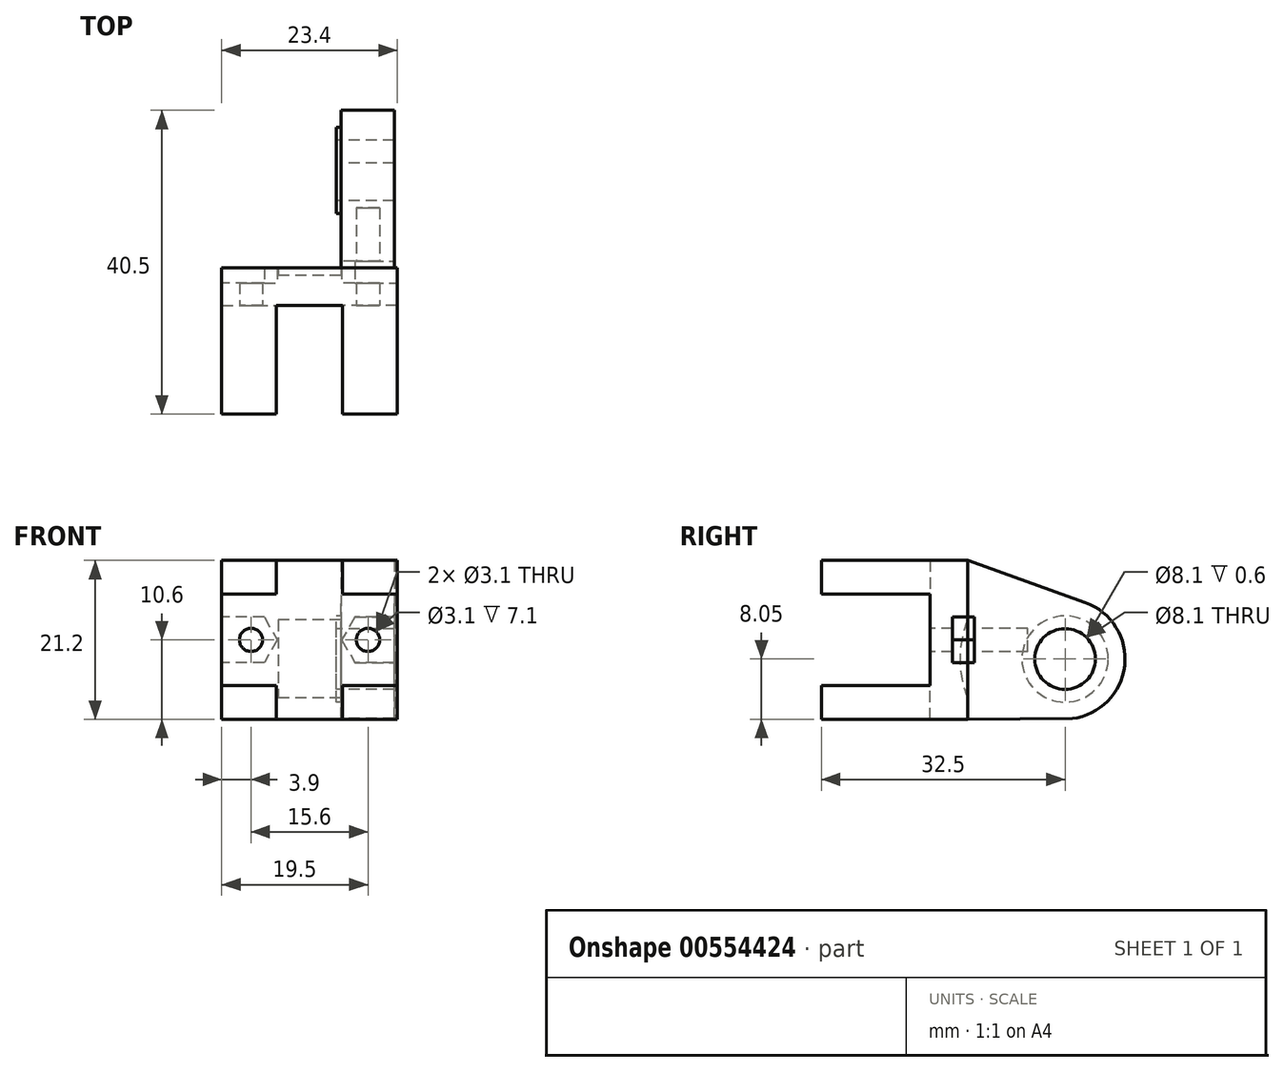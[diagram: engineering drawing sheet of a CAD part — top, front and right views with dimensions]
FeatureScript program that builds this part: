
annotation { "Feature Type Name" : "Feature", "Feature Type Description" : "" }
export const myFeature = defineFeature(function(context is Context, id is Id, definition is map)
    precondition{}
    {
        {
            assignVariable(context, id + "F0", {"name" : "bearing_width", "anyValue" : 7.2});
        }
        {
            assignVariable(context, id + "F1", {"name" : "bearing_bump", "anyValue" : 0.6});
        }
        {
            var Q0;
            Q0=qCreatedBy(makeId("Front.planeOp"),FACE);
            var sketch = newSketch(context, id + "F2", { "sketchPlane" : qUnion([Q0])});
            skLineSegment(sketch, "E0.bottom", {"start": v(-11.7, 10.6) * mm, "end": v(11.7, 10.6) * mm});
            skLineSegment(sketch, "E0.top", {"start": v(-11.7, -10.6) * mm, "end": v(11.7, -10.6) * mm});
            skLineSegment(sketch, "E0.left", {"start": v(-11.7, 10.6) * mm, "end": v(-11.7, -10.6) * mm});
            skLineSegment(sketch, "E0.right", {"start": v(11.7, 10.6) * mm, "end": v(11.7, -10.6) * mm});
            skPoint(sketch, "E0.middle", {"position": v(0, 0) * mm});
            skSolve(sketch);
        }
        {
            var Q0;
            Q0=qSketchRegion(id+"F2",true);
            extrude(context, id + "F3", {"entities" : qUnion([Q0]), "depth" : 5 * mm, "offsetDistance" : 25 * mm});
        }
        {
            var Q0;
            Q0=makeQuery(id+"F3.opExtrude","CAP_FACE",FACE,{"disambiguationData":[OSD([sQuery(id+"F2.wireOp",EDGE,"E0.bottom"),sQuery(id+"F2.wireOp",EDGE,"E0.top"),sQuery(id+"F2.wireOp",EDGE,"E0.left"),sQuery(id+"F2.wireOp",EDGE,"E0.right")])],"isStart":false});
            var sketch = newSketch(context, id + "F4", { "sketchPlane" : qUnion([Q0])});
            skCircle(sketch, "E1", {"center": v(-7.8, 0) * mm, "radius": 1.55 * mm});
            skCircle(sketch, "E2", {"center": v(7.8, 0) * mm, "radius": 1.55 * mm});
            skSolve(sketch);
        }
        {
            var Q0;
            Q0=makeQuery(id+"F3.opExtrude","CAP_FACE",FACE,{"disambiguationData":[OSD([sQuery(id+"F2.wireOp",EDGE,"E0.bottom"),sQuery(id+"F2.wireOp",EDGE,"E0.top"),sQuery(id+"F2.wireOp",EDGE,"E0.left"),sQuery(id+"F2.wireOp",EDGE,"E0.right")])],"isStart":false});
            var sketch = newSketch(context, id + "F5", { "sketchPlane" : qUnion([Q0])});
            skLineSegment(sketch, "E3.bottom", {"start": v(-11.7, 10.6) * mm, "end": v(-4.4, 10.6) * mm});
            skLineSegment(sketch, "E3.top", {"start": v(-11.7, 6.1) * mm, "end": v(-4.4, 6.1) * mm});
            skLineSegment(sketch, "E3.left", {"start": v(-11.7, 10.6) * mm, "end": v(-11.7, 6.1) * mm});
            skLineSegment(sketch, "E3.right", {"start": v(-4.4, 10.6) * mm, "end": v(-4.4, 6.1) * mm});
            skLineSegment(sketch, "E4.bottom", {"start": v(11.7, 10.6) * mm, "end": v(4.4, 10.6) * mm});
            skLineSegment(sketch, "E4.top", {"start": v(11.7, 6.1) * mm, "end": v(4.4, 6.1) * mm});
            skLineSegment(sketch, "E4.left", {"start": v(11.7, 10.6) * mm, "end": v(11.7, 6.1) * mm});
            skLineSegment(sketch, "E4.right", {"start": v(4.4, 10.6) * mm, "end": v(4.4, 6.1) * mm});
            skLineSegment(sketch, "E5.bottom", {"start": v(-11.7, -10.6) * mm, "end": v(-4.4, -10.6) * mm});
            skLineSegment(sketch, "E5.top", {"start": v(-11.7, -6.1) * mm, "end": v(-4.4, -6.1) * mm});
            skLineSegment(sketch, "E5.left", {"start": v(-11.7, -10.6) * mm, "end": v(-11.7, -6.1) * mm});
            skLineSegment(sketch, "E5.right", {"start": v(-4.4, -10.6) * mm, "end": v(-4.4, -6.1) * mm});
            skLineSegment(sketch, "E6.bottom", {"start": v(11.7, -10.6) * mm, "end": v(4.4, -10.6) * mm});
            skLineSegment(sketch, "E6.top", {"start": v(11.7, -6.1) * mm, "end": v(4.4, -6.1) * mm});
            skLineSegment(sketch, "E6.left", {"start": v(11.7, -10.6) * mm, "end": v(11.7, -6.1) * mm});
            skLineSegment(sketch, "E6.right", {"start": v(4.4, -10.6) * mm, "end": v(4.4, -6.1) * mm});
            skSolve(sketch);
        }
        {
            var Q0;
            Q0=qSketchRegion(id+"F5",true);
            extrude(context, id + "F6", {"entities" : qUnion([Q0]), "operationType" : NewBodyOperationType.ADD, "depth" : 14.5 * mm, "offsetDistance" : 25 * mm});
        }
        {
            var Q0;
            Q0=makeQuery(id+"F4.imprint","IMPRINT",FACE,{"disambiguationData":[TD([[makeQuery(id+"F4.imprint","IMPRINT",EDGE,{"derivedFrom":sQuery(id+"F4.wireOp",EDGE,"E1")}),-1.0]])]});
            var sketch = newSketch(context, id + "F7", { "sketchPlane" : qUnion([Q0])});
            skCircle(sketch, "E7.cCircle", {"center": v(-7.8, 0) * mm, "radius": 3.5 * mm, "construction": true});
            skLineSegment(sketch, "E7.4", {"start": v(-6.05, 3.03) * mm, "end": v(-4.3, 0) * mm});
            skLineSegment(sketch, "E7.5", {"start": v(-4.3, 0) * mm, "end": v(-6.05, -3.03) * mm});
            skLineSegment(sketch, "E8.bottom", {"start": v(-6.05, 3.03) * mm, "end": v(-11.7, 3.03) * mm});
            skLineSegment(sketch, "E8.top", {"start": v(-6.05, -3.03) * mm, "end": v(-11.7, -3.03) * mm});
            skLineSegment(sketch, "E8.right", {"start": v(-11.7, 3.03) * mm, "end": v(-11.7, -3.03) * mm});
            skLineSegment(sketch, "E9.MirrorCS", {"start": v(6.05, 3.03) * mm, "end": v(4.3, 0) * mm});
            skCircle(sketch, "E10.MirrorC", {"center": v(7.8, 0) * mm, "radius": 3.5 * mm, "construction": true});
            skLineSegment(sketch, "E11.MirrorCS", {"start": v(6.05, -3.03) * mm, "end": v(11.7, -3.03) * mm});
            skLineSegment(sketch, "E12.MirrorCS", {"start": v(11.7, 3.03) * mm, "end": v(11.7, -3.03) * mm});
            skLineSegment(sketch, "E13.MirrorCS", {"start": v(6.05, 3.03) * mm, "end": v(11.7, 3.03) * mm});
            skLineSegment(sketch, "E14.MirrorCS", {"start": v(4.3, 0) * mm, "end": v(6.05, -3.03) * mm});
            skSolve(sketch);
        }
        {
            var Q0;
            Q0=qCreatedBy(makeId("Right.planeOp"),FACE);
            var sketch = newSketch(context, id + "F8", { "sketchPlane" : qUnion([Q0])});
            skCircle(sketch, "E15", {"center": v(13, -2.55) * mm, "radius": 4.05 * mm});
            skSolve(sketch);
        }
        {
            var Q0;
            Q0=qCreatedBy(makeId("Right.planeOp"),FACE);
            var sketch = newSketch(context, id + "F9", { "sketchPlane" : qUnion([Q0])});
            skArc(sketch, "E16", {"start": v(0, 2.65) * mm, "mid": v(-1, -2.55) * mm, "end": v(0, -7.75) * mm});
            skLineSegment(sketch, "E17", {"start": v(0, 2.65) * mm, "end": v(0, -7.75) * mm});
            skSolve(sketch);
        }
        {
            var Q0;
            Q0=qSketchRegion(id+"F9",true);
            extrude(context, id + "F10", {"entities" : qUnion([Q0]), "operationType" : NewBodyOperationType.REMOVE, "depth" : (getVariable(context, 'bearing_width') / 2 + getVariable(context, 'bearing_bump')) * mm, "offsetDistance" : 25 * mm, "hasSecondDirection" : true, "secondDirectionOppositeDirection" : true, "secondDirectionDepth" : (getVariable(context, 'bearing_width') / 2 + getVariable(context, 'bearing_bump')) * mm});
        }
        {
            var Q0;
            Q0=qCreatedBy(makeId("Right.planeOp"),FACE);
            var sketch = newSketch(context, id + "F11", { "sketchPlane" : qUnion([Q0])});
            skCircle(sketch, "E18", {"center": v(13, -2.55) * mm, "radius": 5.75 * mm});
            skSolve(sketch);
        }
        {
            var Q0;
            Q0=qSketchRegion(id+"F11",true);
            extrude(context, id + "F12", {"entities" : qUnion([Q0]), "operationType" : NewBodyOperationType.ADD, "depth" : ((getVariable(context, 'bearing_width') / 2) + getVariable(context, 'bearing_bump')) * mm, "offsetDistance" : 25 * mm, "hasSecondDirection" : true, "secondDirectionOppositeDirection" : false, "secondDirectionDepth" : (getVariable(context, 'bearing_width') / 2) * mm});
        }
        {
            var Q0;
            Q0=makeQuery(id+"F12.opExtrude","CAP_FACE",FACE,{"disambiguationData":[OSD([sQuery(id+"F11.wireOp",EDGE,"E18")])],"isStart":false});
            var sketch = newSketch(context, id + "F13", { "sketchPlane" : qUnion([Q0])});
            skLineSegment(sketch, "E19", {"start": v(0, 10.6) * mm, "end": v(0, -10.6) * mm});
            skLineSegment(sketch, "E20", {"start": v(0, 10.6) * mm, "end": v(15.7, 4.98) * mm});
            skLineSegment(sketch, "E21", {"start": v(0, -10.6) * mm, "end": v(13.95, -10.5) * mm});
            skArc(sketch, "E22", {"start": v(15.7, 4.98) * mm, "mid": v(20.95, -3.44) * mm, "end": v(13.95, -10.5) * mm});
            skSolve(sketch);
        }
        {
            var Q0;
            Q0=qSketchRegion(id+"F13",true);
            extrude(context, id + "F14", {"entities" : qUnion([Q0]), "depth" : 7.1 * mm, "offsetDistance" : 25 * mm});
        }
        {
            var Q0;
            Q0=makeQuery(id+"F8.imprint","IMPRINT",FACE,{"disambiguationData":[TD([[makeQuery(id+"F8.imprint","IMPRINT",EDGE,{"derivedFrom":sQuery(id+"F8.wireOp",EDGE,"E15")}),1.0]])]});
            extrude(context, id + "F15", {"entities" : qUnion([Q0]), "operationType" : NewBodyOperationType.REMOVE, "endBound" : BoundingType.THROUGH_ALL, "depth" : 2 * mm, "offsetDistance" : 25 * mm});
        }
        {
            var Q0;
            Q0=qSketchRegion(id+"F4",true);
            extrude(context, id + "F16", {"entities" : qUnion([Q0]), "operationType" : NewBodyOperationType.REMOVE, "oppositeDirection" : true, "depth" : 13 * mm, "offsetDistance" : 25 * mm});
        }
        {
            var Q0;
            Q0=qSketchRegion(id+"F7",true);
            extrude(context, id + "F17", {"entities" : qUnion([Q0]), "operationType" : NewBodyOperationType.REMOVE, "oppositeDirection" : true, "depth" : 5.9 * mm, "offsetDistance" : 25 * mm, "hasSecondDirection" : true, "secondDirectionOppositeDirection" : true, "secondDirectionDepth" : 3 * mm});
        }
    });
